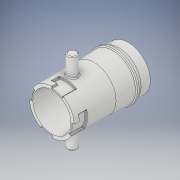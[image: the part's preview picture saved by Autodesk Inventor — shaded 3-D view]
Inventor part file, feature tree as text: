
AUTODESK INVENTOR PART (.ipt)
format: ipt  version: 2019 (Build 230136000, 136)  size: 748,032 bytes
history: native  units: mm
features: other x3, extrude x1, sketch x1
ambient origin geometry x8: Origin, YZ Plane, XZ Plane, XY Plane, X Axis, Y Axis, Z Axis, Center Point
bodies: Solide1 (feature_tree)
feature tree (5):
  other  "canon.ipt"
  extrude  "Extrusion1"  Depth=10.0mm
  other  "Solide1::canon.ipt"
  other  "FonctionRepérage1"
  sketch  "Esquisse1"
